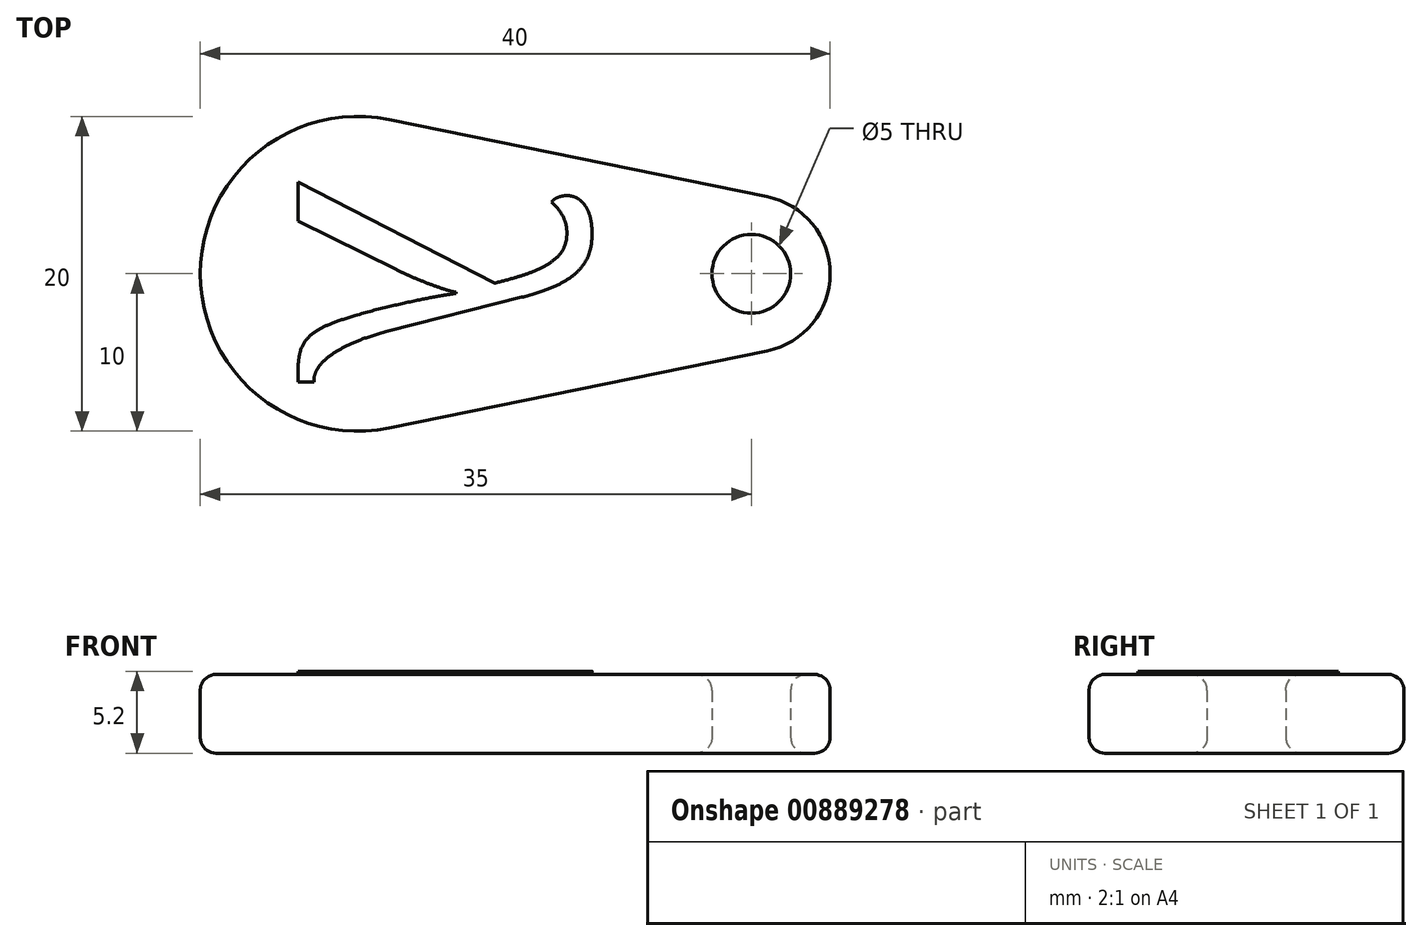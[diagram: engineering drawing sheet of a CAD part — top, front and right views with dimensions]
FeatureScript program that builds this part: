
annotation { "Feature Type Name" : "Feature", "Feature Type Description" : "" }
export const myFeature = defineFeature(function(context is Context, id is Id, definition is map)
    precondition{}
    {
        {
            var Q0;
            Q0=qCreatedBy(makeId("Top.planeOp"),FACE);
            var sketch = newSketch(context, id + "F0", { "sketchPlane" : qUnion([Q0])});
            skCircle(sketch, "E0", {"center": v(0, 0) * mm, "radius": 10 * mm});
            skCircle(sketch, "E1", {"center": v(25, 0) * mm, "radius": 2.5 * mm});
            skCircle(sketch, "E2", {"center": v(25, 0) * mm, "radius": 5 * mm});
            skLineSegment(sketch, "E3", {"start": v(2, 9.8) * mm, "end": v(26, 4.9) * mm});
            skLineSegment(sketch, "E4", {"start": v(2, -9.8) * mm, "end": v(26, -4.9) * mm});
            skText(sketch, "E5", { "text": "λ", "fontName": "NotoSerif-Regular.ttf"});
            const initialGuessF0  = {"E5": [-0.0038, 0.00603, 0, -1, 0.01747]};
            skSetInitialGuess(sketch, initialGuessF0);
            skSolve(sketch);
        }
        {
            var Q0;
            {var subQ0=sQuery(id+"F0.wireOp",EDGE,"E5.sketch_text.stroke-0");Q0=makeQuery(id+"F0.imprint","IMPRINT",FACE,{"disambiguationData":[TD([[makeQuery(id+"F0.imprint","IMPRINT",EDGE,{"derivedFrom":subQ0}),1.0]])]});}
            var Q1;
            {var subQ1=sQuery(id+"F0.wireOp",EDGE,"E5.sketch_text.stroke-0");Q1=makeQuery(id+"F0.imprint","IMPRINT",FACE,{"disambiguationData":[TD([[makeQuery(id+"F0.imprint","IMPRINT",EDGE,{"derivedFrom":subQ1}),-1.0]])]});}
            var Q2;
            {var subQ5=sQuery(id+"F0.wireOp",EDGE,"E5.sketch_text.stroke-2");Q2=makeQuery(id+"F0.imprint","IMPRINT",FACE,{"disambiguationData":[TD([[makeQuery(id+"F0.imprint","IMPRINT",EDGE,{"derivedFrom":subQ5}),-1.0]])]});}
            var Q3;
            {var subQ5=sQuery(id+"F0.wireOp",EDGE,"E3");Q3=makeQuery(id+"F0.imprint","IMPRINT",FACE,{"disambiguationData":[TD([[makeQuery(id+"F0.imprint","IMPRINT",EDGE,{"derivedFrom":subQ5}),-1.0]])]});}
            var Q4;
            Q4=makeQuery(id+"F0.imprint","IMPRINT",FACE,{"disambiguationData":[TD([[makeQuery(id+"F0.imprint","IMPRINT",EDGE,{"derivedFrom":sQuery(id+"F0.wireOp",EDGE,"E1")}),-1.0]])]});
            var Q5;
            {var subQ8=sQuery(id+"F0.wireOp",EDGE,"E5.sketch_text.stroke-17");Q5=makeQuery(id+"F0.imprint","IMPRINT",FACE,{"disambiguationData":[TD([[makeQuery(id+"F0.imprint","IMPRINT",EDGE,{"derivedFrom":subQ8}),1.0]])]});}
            var Q6;
            {var subQ0=sQuery(id+"F0.wireOp",EDGE,"E5.sketch_text.stroke-17");Q6=makeQuery(id+"F0.imprint","IMPRINT",FACE,{"disambiguationData":[TD([[makeQuery(id+"F0.imprint","IMPRINT",EDGE,{"derivedFrom":subQ0}),-1.0]])]});}
            extrude(context, id + "F1", {"entities" : qUnion([Q0, Q1, Q2, Q3, Q4, Q5, Q6]), "depth" : 5 * mm, "offsetDistance" : 25 * mm});
        }
        {
            var Q0;
            {var subQ1=sQuery(id+"F0.wireOp",EDGE,"E5.sketch_text.stroke-0");Q0=makeQuery(id+"F0.imprint","IMPRINT",FACE,{"disambiguationData":[TD([[makeQuery(id+"F0.imprint","IMPRINT",EDGE,{"derivedFrom":subQ1}),-1.0]])]});}
            var Q1;
            {var subQ5=sQuery(id+"F0.wireOp",EDGE,"E5.sketch_text.stroke-2");Q1=makeQuery(id+"F0.imprint","IMPRINT",FACE,{"disambiguationData":[TD([[makeQuery(id+"F0.imprint","IMPRINT",EDGE,{"derivedFrom":subQ5}),-1.0]])]});}
            var Q2;
            {var subQ0=sQuery(id+"F0.wireOp",EDGE,"E5.sketch_text.stroke-17");Q2=makeQuery(id+"F0.imprint","IMPRINT",FACE,{"disambiguationData":[TD([[makeQuery(id+"F0.imprint","IMPRINT",EDGE,{"derivedFrom":subQ0}),-1.0]])]});}
            extrude(context, id + "F2", {"entities" : qUnion([Q0, Q1, Q2]), "operationType" : NewBodyOperationType.ADD, "depth" : 5.2 * mm, "offsetDistance" : 25 * mm});
        }
        {
            var Q0;
            Q0=makeQuery(id+"F1.opExtrude","CAP_EDGE",EDGE,{"disambiguationData":[OSD([sQuery(id+"F0.wireOp",EDGE,"E4")])],"isStart":true});
            var Q1;
            Q1=makeQuery(id+"F1.opExtrude","CAP_EDGE",EDGE,{"disambiguationData":[OSD([sQuery(id+"F0.wireOp",EDGE,"E4")])],"isStart":false});
            var Q2;
            Q2=makeQuery(id+"F1.opExtrude","CAP_EDGE",EDGE,{"disambiguationData":[OSD([sQuery(id+"F0.wireOp",EDGE,"E1")])],"isStart":false});
            var Q3;
            Q3=makeQuery(id+"F1.opExtrude","CAP_EDGE",EDGE,{"disambiguationData":[OSD([sQuery(id+"F0.wireOp",EDGE,"E1")])],"isStart":true});
            fillet(context, id + "F3", {"entities" : qUnion([Q0, Q1, Q2, Q3]), "radius" : 1 * mm, "tangentPropagation" : true, "allowEdgeOverflow" : false});
        }
    });
